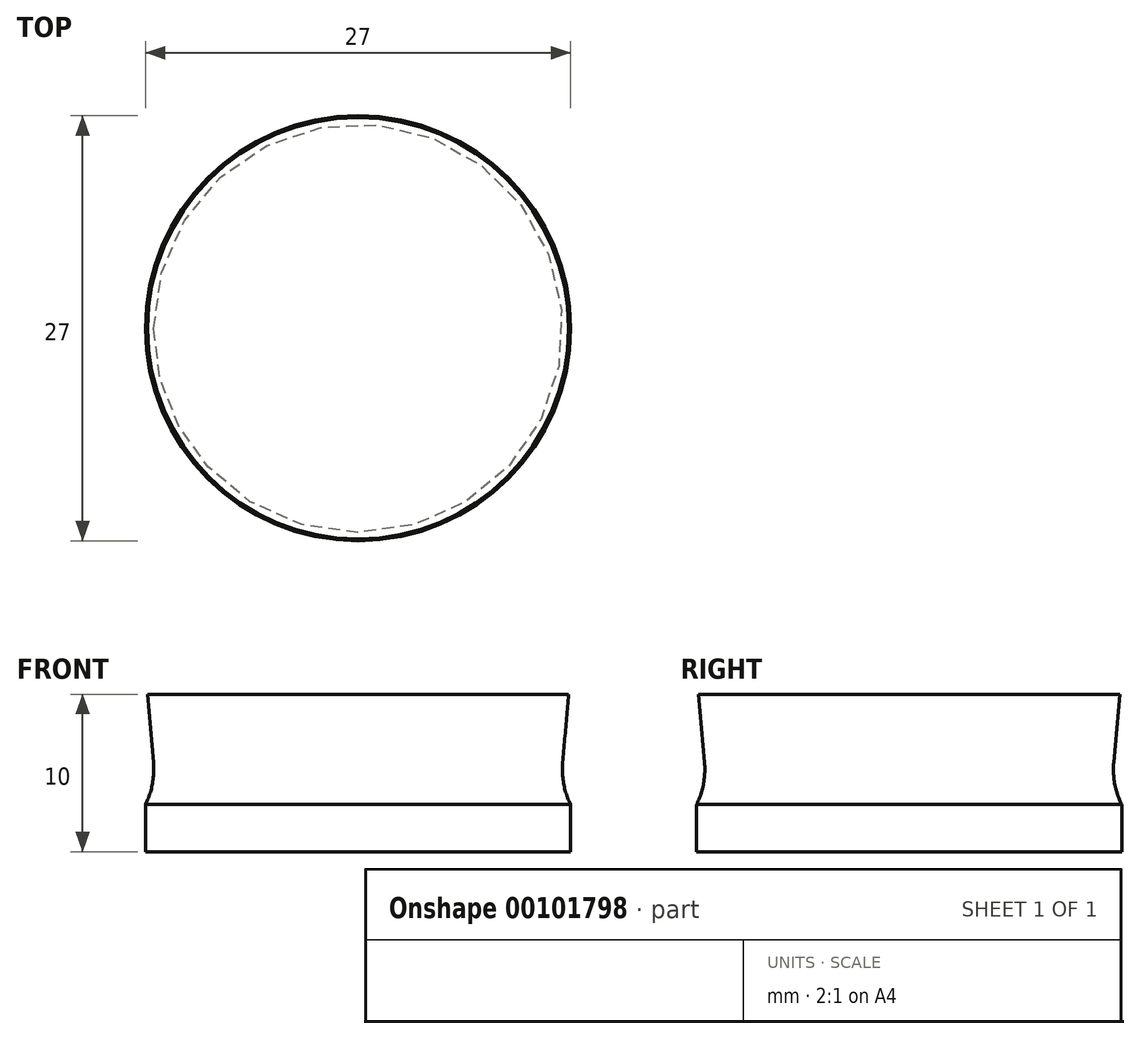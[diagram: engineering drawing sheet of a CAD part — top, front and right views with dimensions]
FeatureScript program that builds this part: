
annotation { "Feature Type Name" : "Feature", "Feature Type Description" : "" }
export const myFeature = defineFeature(function(context is Context, id is Id, definition is map)
    precondition{}
    {
        {
            var Q0;
            Q0=qCreatedBy(makeId("Top.planeOp"),FACE);
            var sketch = newSketch(context, id + "F0", { "sketchPlane" : qUnion([Q0])});
            skCircle(sketch, "E0", {"center": v(0, 0) * mm, "radius": 12.5 * mm});
            skSolve(sketch);
        }
        {
            var Q0;
            Q0 = qSketchRegion(id + "F0", true);
            extrude(context, id + "F1", {"entities" : qUnion([Q0]), "depth" : 10 * mm, "hasDraft" : true, "draftAngle" : 5 * degree});
        }
        {
            var Q0;
            Q0=makeQuery(id+"F1.opExtrude","CAP_FACE",FACE,{"disambiguationData":[OSD([sQuery(id+"F0.wireOp",EDGE,"E0")])],"isStart":true});
            var sketch = newSketch(context, id + "F2", { "sketchPlane" : qUnion([Q0])});
            skCircle(sketch, "E1", {"center": v(0, 0) * mm, "radius": 13.5 * mm});
            skSolve(sketch);
        }
        {
            var Q0;
            Q0 = qSketchRegion(id + "F2", true);
            extrude(context, id + "F3", {"entities" : qUnion([Q0]), "operationType" : NewBodyOperationType.ADD, "oppositeDirection" : true, "depth" : 3 * mm});
        }
        {
            var Q0;
            Q0=makeQuery(id+"F3.boolean.opBoolean","INTERSECT",EDGE,{"derivedFrom":[makeQuery(id+"F1.opExtrude","SWEPT_FACE",FACE,{"disambiguationData":[OSD([sQuery(id+"F0.wireOp",EDGE,"E0")])]}),makeQuery(id+"F3.opExtrude","CAP_FACE",FACE,{"disambiguationData":[OSD([sQuery(id+"F2.wireOp",EDGE,"E1")])],"isStart":false})]});
            fillet(context, id + "F4", {"entities" : qUnion([Q0]), "radius" : 5 * mm, "tangentPropagation" : true, "allowEdgeOverflow" : false});
        }
    });
